# Revit family: Drapery_System-Lutron-Alena-LOD_200
name_source: partatom
category: Generic Models
revit_build: Autodesk Revit 2017 (Build: 20160720_1515(x64)
units: mm (PartAtom-declared; Revit-internal decimal feet)

## family parameters
Always vertical = Yes
Can host rebar = No
Cut with Voids When Loaded = No
OmniClass Number = 23.25.40.17.11
OmniClass Title = Horizontally Sliding Partitions
Part Type = Normal
Room Calculation Point = No
Round Connector Dimension = Use Diameter
Shared = No
Work Plane-Based = No

## types (6) — shared parameters
Alena = Yes
Alena QS = No
Alena QS Wireless = No
Assembly Code = C1010300
Description = Drapery System
Instruction Sheet Link = http://www.lutron.com
Manufacturer = Lutron Electronics Co., Inc
Manufacturer Fax Number = (610) 282-1243
Model = Alena
Product Documentation Link = http://www.lutron.com
Product Name = Alean Pull-to-Start Drapery Track
Product Page URL = http://www.lutron.com
Track = Metal - Lutron - Steel
URL = www.lutron.com
Version = 2017 - v1.0a
Video Link = https://www.youtube.com
Warranty URL = http://www.lutron.com
zero-valued in all types: Cost

## per-type parameters (varying)
| type | Auxiliary Car Spacing | Drapery | Panel Wavelength | Performance URL | Pinch Pleat | Ripplefold | Track Offset Constraint | Type Comments |
| Pinch Pleat 2.5x | 3 1/2" | Fabric - Pinch Pleat - 2x | 7" | http://www.lutron.com | Yes | No | 1/8" | Pinch Pleat |
| Pinch Pleat 3x | 3" | Fabric - Pinch Pleat - 3x | 6" |  | Yes | No | 1/8" | Pinch Pleat |
| Ripplefold 120% | 1 7/8" | Fabric - Ripplefold - 120% | 3 3/4" |  | No | Yes | 1/4" | Ripplefold |
| Ripplefold 80% | 2 3/8" | Fabric - Ripplefold - 80% | 4 3/4" |  | No | Yes | 1/4" | Ripplefold |
| Pinch Pleat 2x | 3 1/2" | Fabric - Pinch Pleat - 2x | 7" |  | Yes | No | 1/8" | Pinch Pleat |
| Ripplefold 100% | 2 1/8" | Fabric - Ripplefold - 100% | 4 1/4" |  | No | Yes | 1/4" | Ripplefold |

type visibility flags: 6 boolean params named "<type name>" — each type sets only its own to Yes (folded from table)

## geometry (parser evidence)
native form markers: Sweep x11
no freeform markers — native parametric forms only
